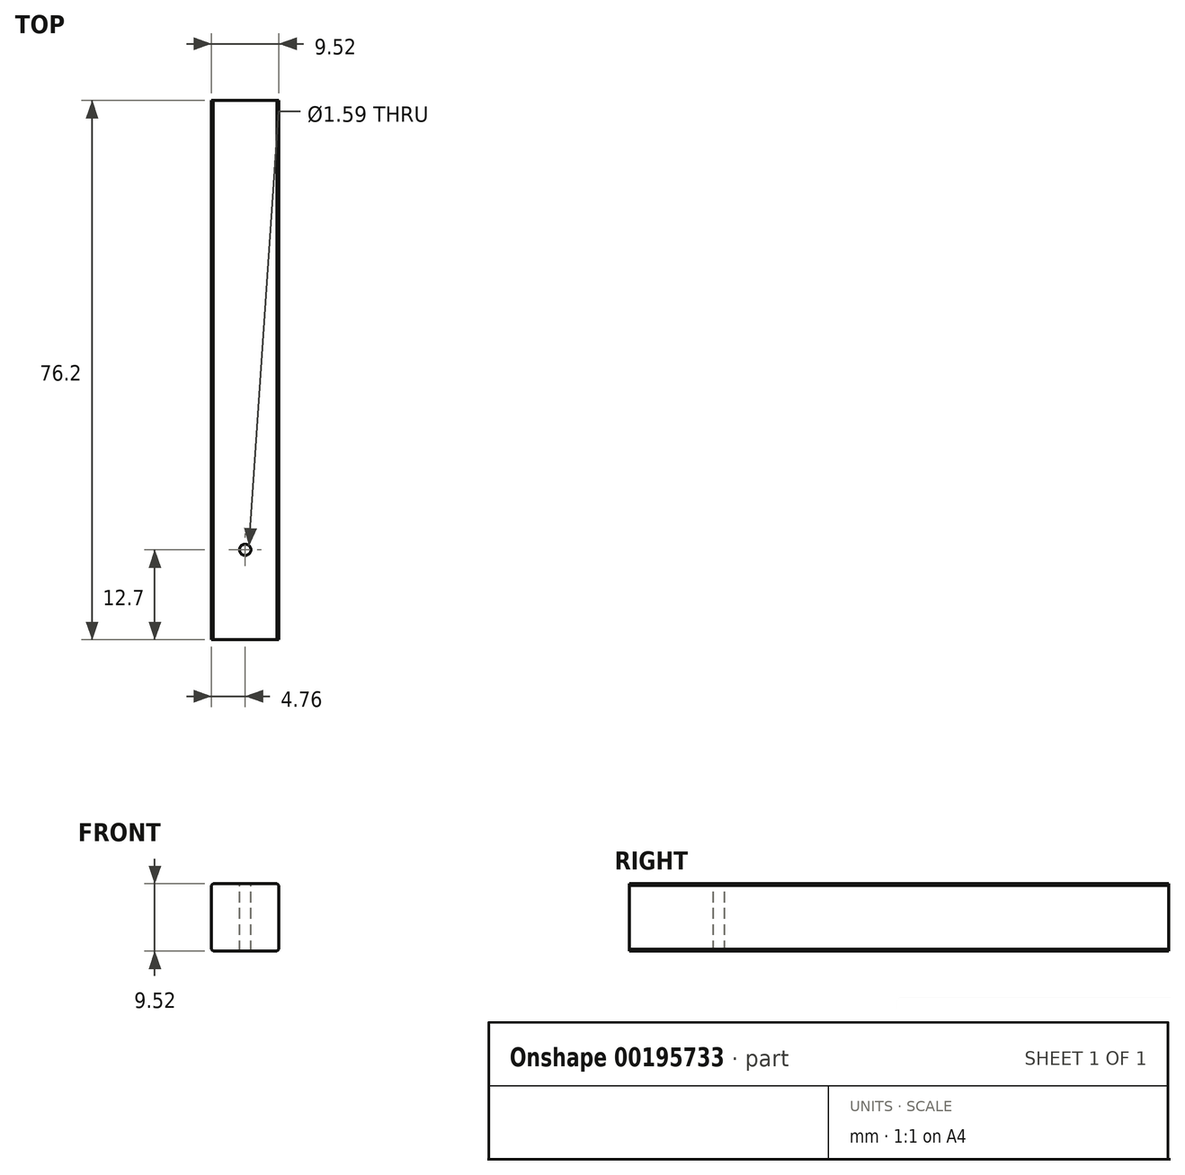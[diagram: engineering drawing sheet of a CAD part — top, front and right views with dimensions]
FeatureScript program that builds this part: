
annotation { "Feature Type Name" : "Feature", "Feature Type Description" : "" }
export const myFeature = defineFeature(function(context is Context, id is Id, definition is map)
    precondition{}
    {
        {
            var Q0;
            Q0=qCreatedBy(makeId("Front.planeOp"),FACE);
            var sketch = newSketch(context, id + "F0", { "sketchPlane" : qUnion([Q0])});
            skLineSegment(sketch, "E0.bottom", {"start": v(4.76, 4.76) * mm, "end": v(-4.76, 4.76) * mm});
            skLineSegment(sketch, "E0.top", {"start": v(4.76, -4.76) * mm, "end": v(-4.76, -4.76) * mm});
            skLineSegment(sketch, "E0.left", {"start": v(4.76, 4.76) * mm, "end": v(4.76, -4.76) * mm});
            skLineSegment(sketch, "E0.right", {"start": v(-4.76, 4.76) * mm, "end": v(-4.76, -4.76) * mm});
            skPoint(sketch, "E0.middle", {"position": v(0, 0) * mm});
            skSolve(sketch);
        }
        {
            var Q0;
            Q0 = qSketchRegion(id + "F0", true);
            extrude(context, id + "F1", {"entities" : qUnion([Q0]), "depth" : 76.2 * mm});
        }
        {
            var Q0;
            Q0=makeQuery(id+"F1.opExtrude","SWEPT_EDGE",EDGE,{"disambiguationData":[OSD([sQuery(id+"F0.wireOp",EDGE,"E0.bottom"),sQuery(id+"F0.wireOp",EDGE,"E0.right")])]});
            var Q1;
            Q1=makeQuery(id+"F1.opExtrude","SWEPT_EDGE",EDGE,{"disambiguationData":[OSD([sQuery(id+"F0.wireOp",EDGE,"E0.top"),sQuery(id+"F0.wireOp",EDGE,"E0.right")])]});
            var Q2;
            Q2=makeQuery(id+"F1.opExtrude","SWEPT_EDGE",EDGE,{"disambiguationData":[OSD([sQuery(id+"F0.wireOp",EDGE,"E0.bottom"),sQuery(id+"F0.wireOp",EDGE,"E0.left")])]});
            var Q3;
            Q3=makeQuery(id+"F1.opExtrude","SWEPT_EDGE",EDGE,{"disambiguationData":[OSD([sQuery(id+"F0.wireOp",EDGE,"E0.top"),sQuery(id+"F0.wireOp",EDGE,"E0.left")])]});
            chamfer(context, id + "F2", {"entities" : qUnion([Q0, Q1, Q2, Q3]), "width" : 0.25 * mm, "tangentPropagation" : true});
        }
        {
            var Q0;
            Q0=makeQuery(id+"F1.opExtrude","SWEPT_FACE",FACE,{"disambiguationData":[OSD([sQuery(id+"F0.wireOp",EDGE,"E0.bottom")])]});
            var sketch = newSketch(context, id + "F3", { "sketchPlane" : qUnion([Q0])});
            skLineSegment(sketch, "E1", {"start": v(0, -76.2) * mm, "end": v(0, -63.5) * mm});
            skPoint(sketch, "E1.endSnap0", {"position": v(0, -76.2) * mm});
            skCircle(sketch, "E2", {"center": v(0, -63.5) * mm, "radius": 0.8 * mm});
            skSolve(sketch);
        }
        {
            var Q0;
            Q0 = qSketchRegion(id + "F3", true);
            extrude(context, id + "F4", {"entities" : qUnion([Q0]), "operationType" : NewBodyOperationType.REMOVE, "oppositeDirection" : true, "depth" : 25.4 * mm});
        }
    });
